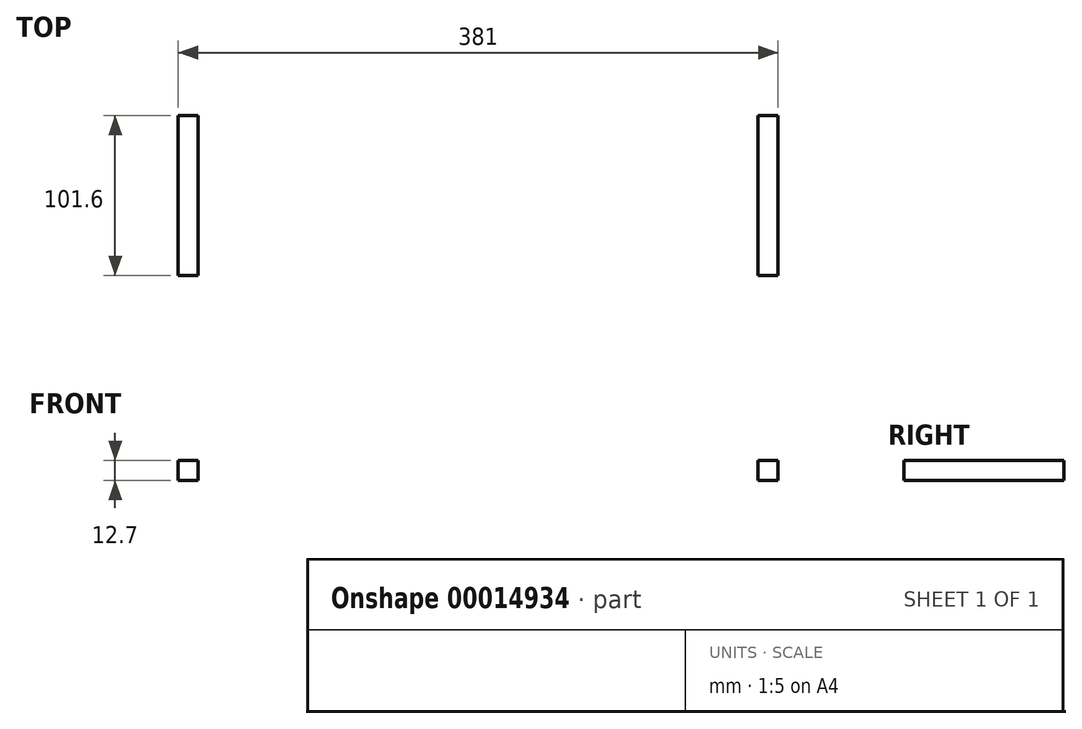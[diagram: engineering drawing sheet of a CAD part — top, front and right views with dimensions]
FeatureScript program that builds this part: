
annotation { "Feature Type Name" : "Feature", "Feature Type Description" : "" }
export const myFeature = defineFeature(function(context is Context, id is Id, definition is map)
    precondition{}
    {
        {
            var Q0;
            Q0=qCreatedBy(makeId("Top.planeOp"),FACE);
            var sketch = newSketch(context, id + "F0", { "sketchPlane" : qUnion([Q0])});
            skLineSegment(sketch, "E0.bottom", {"start": v(0, 571.5) * mm, "end": v(381, 571.5) * mm});
            skLineSegment(sketch, "E0.top", {"start": v(0, 0) * mm, "end": v(381, 0) * mm});
            skLineSegment(sketch, "E0.left", {"start": v(0, 571.5) * mm, "end": v(0, 0) * mm});
            skLineSegment(sketch, "E0.right", {"start": v(381, 571.5) * mm, "end": v(381, 0) * mm});
            skLineSegment(sketch, "E1.bottom", {"start": v(0, 139.7) * mm, "end": v(76.2, 139.7) * mm});
            skLineSegment(sketch, "E1.top", {"start": v(0, 190.5) * mm, "end": v(76.2, 190.5) * mm});
            skLineSegment(sketch, "E1.left", {"start": v(0, 139.7) * mm, "end": v(0, 190.5) * mm});
            skLineSegment(sketch, "E1.right", {"start": v(76.2, 139.7) * mm, "end": v(76.2, 190.5) * mm});
            skLineSegment(sketch, "E2.bottom", {"start": v(381, 139.7) * mm, "end": v(304.8, 139.7) * mm});
            skLineSegment(sketch, "E2.top", {"start": v(381, 190.5) * mm, "end": v(304.8, 190.5) * mm});
            skLineSegment(sketch, "E2.left", {"start": v(381, 139.7) * mm, "end": v(381, 190.5) * mm});
            skLineSegment(sketch, "E2.right", {"start": v(304.8, 139.7) * mm, "end": v(304.8, 190.5) * mm});
            skLineSegment(sketch, "E3.bottom", {"start": v(0, 571.5) * mm, "end": v(12.7, 571.5) * mm});
            skLineSegment(sketch, "E3.top", {"start": v(0, 469.9) * mm, "end": v(12.7, 469.9) * mm});
            skLineSegment(sketch, "E3.left", {"start": v(0, 571.5) * mm, "end": v(0, 469.9) * mm});
            skLineSegment(sketch, "E3.right", {"start": v(12.7, 571.5) * mm, "end": v(12.7, 469.9) * mm});
            skLineSegment(sketch, "E4.bottom", {"start": v(368.3, 571.5) * mm, "end": v(381, 571.5) * mm});
            skLineSegment(sketch, "E4.top", {"start": v(368.3, 469.9) * mm, "end": v(381, 469.9) * mm});
            skLineSegment(sketch, "E4.left", {"start": v(368.3, 571.5) * mm, "end": v(368.3, 469.9) * mm});
            skLineSegment(sketch, "E4.right", {"start": v(381, 571.5) * mm, "end": v(381, 469.9) * mm});
            skLineSegment(sketch, "E5", {"start": v(0, 50.8) * mm, "end": v(76.2, 139.7) * mm});
            skLineSegment(sketch, "E6", {"start": v(304.8, 139.7) * mm, "end": v(381, 50.8) * mm});
            skPoint(sketch, "E7", {"position": v(51.4, 110.77) * mm});
            skPoint(sketch, "E8", {"position": v(329.6, 110.77) * mm});
            skLineSegment(sketch, "E9", {"start": v(76.2, 139.7) * mm, "end": v(76.2, 110.77) * mm});
            skLineSegment(sketch, "E10", {"start": v(51.4, 110.77) * mm, "end": v(76.2, 110.77) * mm});
            skLineSegment(sketch, "E11", {"start": v(304.8, 139.7) * mm, "end": v(304.8, 110.77) * mm});
            skLineSegment(sketch, "E12", {"start": v(329.6, 110.77) * mm, "end": v(304.8, 110.77) * mm});
            skSolve(sketch);
        }
        {
            var Q0;
            Q0=makeQuery(id+"F0.imprint","IMPRINT",FACE,{"disambiguationData":[TD([[makeQuery(id+"F0.imprint","IMPRINT",EDGE,{"derivedFrom":sQuery(id+"F0.wireOp",EDGE,"E0.bottom")}),-1.0]])]});
            extrude(context, id + "F1", {"entities" : qUnion([Q0]), "depth" : 12.7 * mm});
        }
    });
